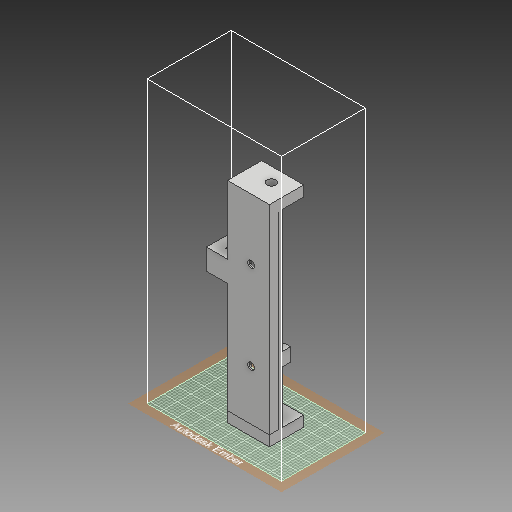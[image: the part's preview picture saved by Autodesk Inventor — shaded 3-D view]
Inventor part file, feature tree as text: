
AUTODESK INVENTOR PART (.ipt)
format: ipt  version: 2018 (Build 220112000, 112)  size: 801,792 bytes
history: native  units: mm
features: sketch x69, extrude x52, hole x8, fillet x7
ambient origin geometry x8: Origin, YZ Plane, XZ Plane, XY Plane, X Axis, Y Axis, Z Axis, Center Point
bodies: Solid1 (feature_tree)
feature tree (136):
  extrude  "Extrusion1"  Depth=100.0mm
  extrude  "Extrusion2"  Depth=5.0mm
  sketch  "Sketch3"  dims[d5=5.0mm d6=40.0mm d7=0.0mm]
  hole  "Hole1"  [1 undecoded]
  extrude  "Extrusion3"  Depth=2.0mm
  hole  "Hole2"  [1 undecoded]
  fillet  "Fillet1"  Radius=8.5mm
  extrude  "Extrusion4"  TaperAngle=90.0deg  [1 undecoded]
  extrude  "Extrusion5"  TaperAngle=180.0deg  [1 undecoded]
  hole  "Hole3"  [1 undecoded]
  fillet  "Fillet2"  Radius=3.5mm
  extrude  "Extrusion6"  Depth=10.0mm
  extrude  "Extrusion7"  Depth=5.0mm TaperAngle=0.0deg
  extrude  "Extrusion8"  Depth=5.0mm TaperAngle=0.0deg
  extrude  "Extrusion9"  Depth=0.1mm
  hole  "Hole4"  [1 undecoded]
  extrude  "Extrusion10"  Depth=5.5mm
  hole  "Hole5"  [1 undecoded]
  extrude  "Extrusion11"  Depth=2.1mm TaperAngle=0.0deg
  extrude  "Extrusion12"  Depth=5.0mm
  extrude  "Extrusion13"  Depth=1.0mm TaperAngle=0.0deg
  extrude  "Extrusion14"  Depth=3.8mm TaperAngle=0.0deg
  sketch  "Sketch21"  dims[d66=6.35mm d67=3.8mm d68=0.0mm]
  extrude  "Extrusion15"  Depth=8.0mm TaperAngle=0.0deg
  sketch  "Sketch23"  dims[d78=3.3mm d79=6.0mm d80=4.0mm d81=2.0mm d82=90.0deg d83=80.0mm d84=20.594885mm d85=5.45mm]
  extrude  "Extrusion16"  Depth=2.0mm
  extrude  "Extrusion17"  Depth=10.5mm
  hole  "Hole6"  [1 undecoded]
  fillet  "Fillet3"  Radius=4.5mm
  extrude  "Extrusion18"  Depth=8.0mm TaperAngle=0.0deg
  sketch  "Sketch28"  dims[d100=4.1mm d101=0.0mm d102=5.0mm]
  extrude  "Extrusion19"  Depth=10.0mm
  extrude  "Extrusion20"  Depth=5.0mm
  extrude  "Extrusion21"  Depth=10.0mm TaperAngle=0.0deg
  hole  "Hole7"  [1 undecoded]
  extrude  "Extrusion22"  Depth=21.0mm
  extrude  "Extrusion23"  Depth=118.0mm TaperAngle=0.0deg
  fillet  "Fillet4"  Radius=50.0mm
  fillet  "Fillet5"  Radius=7.499983mm
  extrude  "Extrusion24"  Depth=10.0mm
  extrude  "Extrusion25"  Depth=4.1mm TaperAngle=0.0deg
  hole  "Hole8"  [1 undecoded]
  extrude  "Extrusion26"  Depth=8.0mm TaperAngle=0.0deg
  sketch  "Sketch39"  dims[d142=3.85mm d143=0.0mm d144=3.0mm]
  extrude  "Extrusion27"  Depth=1.0mm
  extrude  "Extrusion28"  Depth=3.0mm
  extrude  "Extrusion29"  Depth=100.0mm TaperAngle=0.0deg
  extrude  "Extrusion30"  Depth=10.0mm
  extrude  "Extrusion31"  Depth=5.0mm
  fillet  "Fillet6"  Radius=7.5mm
  extrude  "Extrusion32"  Depth=8.0mm
  sketch  "Sketch46"  dims[d167=2.0mm d168=0.0mm d169=2.0mm d170=0.0mm]
  extrude  "Extrusion33"  Depth=5.0mm TaperAngle=0.0deg
  sketch  "Sketch48"  dims[d174=3.3mm d175=10.0mm d176=0.0mm]
  extrude  "Extrusion34"  Depth=2.0mm TaperAngle=0.0deg
  extrude  "Extrusion35"  Depth=2.0mm
  sketch  "Sketch51"  dims[d182=5.0mm d183=9.5mm d184=0.0mm]
  extrude  "Extrusion36"  Depth=10.0mm TaperAngle=0.0deg
  sketch  "Sketch53"  dims[d189=5.0mm d190=3.5mm]
  extrude  "Extrusion37"  Depth=2.0mm
  sketch  "Sketch55"  dims[d194=8.5mm d195=12.0mm]
  extrude  "Extrusion38"  Depth=5.0mm
  extrude  "Extrusion39"  Depth=9.5mm TaperAngle=0.0deg
  extrude  "Extrusion40"  Depth=9.5mm TaperAngle=0.0deg
  extrude  "Extrusion41"  Depth=5.0mm
  extrude  "Extrusion42"  Depth=9.5mm TaperAngle=0.0deg
  extrude  "Extrusion43"  Depth=12.0mm
  extrude  "Extrusion44"  Depth=12.0mm
  extrude  "Extrusion45"  Depth=3.5mm TaperAngle=0.0deg
  extrude  "Extrusion46"  Depth=3.5mm TaperAngle=0.0deg
  extrude  "Extrusion47"  Depth=3.2mm TaperAngle=0.0deg
  extrude  "Extrusion48"  Depth=3.2mm TaperAngle=0.0deg
  extrude  "Extrusion49"  Depth=101.0mm TaperAngle=0.0deg
  extrude  "Extrusion50"  Depth=4.0mm
  fillet  "Fillet7"  Radius=4.0mm
  extrude  "Extrusion51"  Depth=106.25mm TaperAngle=0.0deg
  extrude  "Extrusion52"  Depth=1.8mm TaperAngle=0.0deg
  sketch  "Sketch1"  dims[d0=22.65mm d1=100.0mm]
  sketch  "Sketch2"  dims[d2=5.0mm d3=0.0mm d4=5.0mm]
  sketch  "Sketch4"  dims[d8=10.0mm]
  sketch  "Sketch5"  dims[d9=4.0mm d10=6.0mm d11=4.0mm d12=2.0mm d13=90.0deg d14=115.0mm d15=20.594885mm d16=23.0mm]
  sketch  "Sketch6"  dims[d17=102.75mm d18=0.0mm d19=1.175mm d20=8.5mm]
  sketch  "Sketch7"  dims[d21=21.0mm d22=90.0deg]
  sketch  "Sketch8"  dims[d23=8.5mm d24=180.0deg]
  sketch  "Sketch9"  dims[d25=21.0mm]
  sketch  "Sketch10"  dims[d26=4.0mm d27=6.0mm d28=4.0mm d29=2.0mm d30=90.0deg d31=115.0mm d32=20.594885mm d33=1.0mm d34=3.5mm]
  sketch  "Sketch11"  dims[d35=15.825mm d36=10.0mm]
  sketch  "Sketch12"  dims[d37=10.0mm d38=5.0mm d39=0.0mm]
  sketch  "Sketch13"  dims[d40=5.0mm d41=12.5mm d42=0.0mm]
  sketch  "Sketch14"  dims[d43=6.0mm d44=6.0mm d45=4.0mm d46=2.0mm d47=90.0deg d48=115.0mm d49=20.594885mm d50=0.1mm]
  sketch  "Sketch15"  dims[d51=4.25mm d52=1000.0mm d53=0.0mm]
  sketch  "Sketch16"  dims[d54=3.3mm d55=5.5mm]
  sketch  "Sketch17"  dims[d56=3.2mm d57=3.0mm]
  sketch  "Sketch18"  dims[d58=2.1mm d59=91.25mm d60=0.0mm]
  sketch  "Sketch19"  dims[d61=4.44mm d62=5.0mm]
  sketch  "Sketch20"  dims[d63=1.0mm d64=91.25mm d65=0.0mm]
  sketch  "Sketch22"  dims[d69=3.3mm d70=6.0mm d71=4.0mm d72=2.0mm d73=90.0deg d74=8.0mm d75=20.594885mm d76=4.55mm d77=0.0mm]
  sketch  "Sketch24"  dims[d86=129.8mm d87=0.0mm d88=10.5mm]
  sketch  "Sketch25"  dims[d89=2.5mm d90=0.0mm d91=10.0mm d92=4.5mm d93=0.0mm]
  sketch  "Sketch26"  dims[d94=8.0mm d95=0.0mm d96=15.5mm d97=0.0mm]
  sketch  "Sketch27"  dims[d98=10.0mm d99=10.0mm]
  sketch  "Sketch29"  dims[d103=17.5mm d104=10.0mm d105=0.0mm]
  sketch  "Sketch30"  dims[d106=5.0mm]
  sketch  "Sketch31"  dims[d107=6.0mm d108=6.0mm d109=4.0mm d110=2.0mm d111=90.0deg d112=80.0mm d113=20.594885mm d114=2.0mm]
  sketch  "Sketch32"  dims[d115=45.0mm d116=0.0mm d117=21.0mm]
  sketch  "Sketch33"  dims[d118=4.5mm d119=118.0mm d120=0.0mm d121=50.0mm d122=7.499983mm]
  sketch  "Sketch34"  dims[d123=7.5mm d124=10.0mm]
  sketch  "Sketch35"  dims[d125=10.0mm d126=4.1mm d127=0.0mm]
  sketch  "Sketch36"  dims[d128=13.4mm d129=0.0mm d130=5.0mm]
  sketch  "Sketch37"  dims[d131=6.0mm d132=6.0mm d133=4.0mm d134=2.0mm d135=90.0deg d136=8.0mm d137=20.594885mm d138=130.4mm d139=0.0mm]
  sketch  "Sketch38"  dims[d140=1.0mm d141=1.0mm]
  sketch  "Sketch40"  dims[d145=2.0mm d146=100.0mm d147=0.0mm]
  sketch  "Sketch41"  dims[d148=4.0mm d149=10.0mm]
  sketch  "Sketch42"  dims[d150=5.0mm d151=15.0mm d152=7.5mm]
  sketch  "Sketch43"  dims[d153=7.5mm d154=0.0mm]
  sketch  "Sketch44"  dims[d155=6.0mm d156=6.0mm d157=4.0mm d158=2.0mm d159=90.0deg d160=8.0mm d161=20.594885mm d162=5.5mm]
  sketch  "Sketch45"  dims[d163=5.0mm d164=0.0mm d165=5.5mm d166=0.0mm]
  sketch  "Sketch47"  dims[d171=2.0mm d172=0.0mm d173=20.0mm]
  sketch  "Sketch49"  dims[d177=2.0mm d178=3.5mm]
  sketch  "Sketch50"  dims[d179=5.0mm d180=0.0mm d181=8.5mm]
  sketch  "Sketch52"  dims[d185=9.5mm d186=0.0mm d187=2.7mm d188=0.0mm]
  sketch  "Sketch54"  dims[d191=7.5mm d192=9.5mm d193=0.0mm]
  sketch  "Sketch56"  dims[d196=10.25mm d197=0.0mm d198=12.0mm]
  sketch  "Sketch57"  dims[d199=10.25mm d200=0.0mm d201=3.5mm d202=0.0mm]
  sketch  "Sketch58"  dims[d203=3.75mm d204=3.5mm d205=0.0mm]
  sketch  "Sketch59"  dims[d206=9.6mm d207=3.2mm d208=0.0mm]
  sketch  "Sketch60"  dims[d209=9.6mm d210=3.2mm d211=0.0mm]
  sketch  "Sketch61"  dims[d212=5.5mm d213=101.0mm d214=0.0mm]
  sketch  "Sketch62"  dims[d215=3.5mm d216=0.0mm d217=4.0mm d218=4.0mm d219=0.0mm]
  sketch  "Sketch63"  dims[d220=9.7mm d221=106.25mm d222=0.0mm]
  sketch  "Sketch64"  dims[d223=9.8mm d224=1.8mm d225=0.0mm]
  sketch  "Sketch65"  dims[d226=9.8mm]
  sketch  "Sketch66"  dims[d227=1.8mm d228=0.0mm]
  sketch  "Sketch67"  dims[d229=5.0mm]
  sketch  "Sketch68"  dims[d230=180.0mm d231=0.0mm]
  sketch  "Sketch69"  dims[d232=2.875mm d233=2.875mm d234=3.0mm d235=3.0mm d236=5.0mm d237=0.0mm d238=1.0mm d239=4.5mm d240=5.0mm d241=0.0mm d242=4.5mm d243=5.0mm d244=0.0mm]
note: 10 required parameter values undecoded (feature->parameter linkage not recoverable at this tier; creation-order binding heuristic only, values carry confidence <= 0.55)
